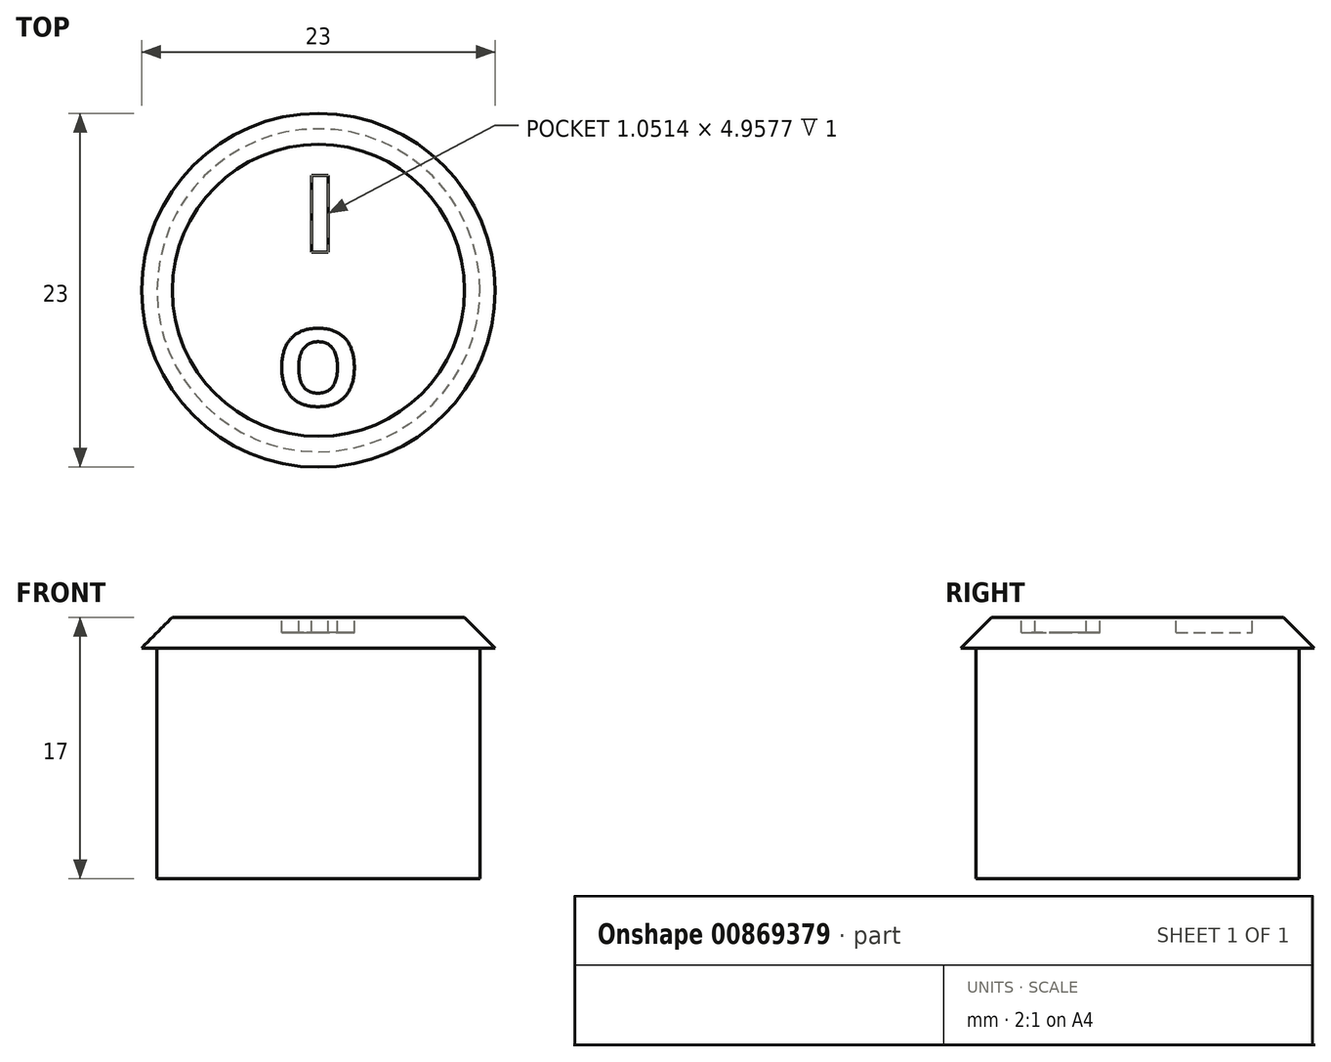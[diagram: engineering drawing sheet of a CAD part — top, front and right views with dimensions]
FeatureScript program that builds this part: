
annotation { "Feature Type Name" : "Feature", "Feature Type Description" : "" }
export const myFeature = defineFeature(function(context is Context, id is Id, definition is map)
    precondition{}
    {
        {
            var Q0;
            Q0=qCreatedBy(makeId("Front.planeOp"),FACE);
            var sketch = newSketch(context, id + "F0", { "sketchPlane" : qUnion([Q0])});
            skLineSegment(sketch, "E0", {"start": v(0, 17) * mm, "end": v(9.5, 17) * mm});
            skLineSegment(sketch, "E1", {"start": v(9.5, 17) * mm, "end": v(11.5, 15) * mm});
            skLineSegment(sketch, "E2", {"start": v(11.5, 15) * mm, "end": v(10.5, 15) * mm});
            skLineSegment(sketch, "E3", {"start": v(10.5, 15) * mm, "end": v(10.5, 0) * mm});
            skLineSegment(sketch, "E4", {"start": v(10.5, 0) * mm, "end": v(0, 0) * mm});
            skLineSegment(sketch, "E5", {"start": v(0, 0) * mm, "end": v(0, 17) * mm});
            skSolve(sketch);
        }
        {
            var Q0;
            Q0=makeQuery(id+"F0.imprint","IMPRINT",FACE,{"disambiguationData":[TD([[makeQuery(id+"F0.imprint","IMPRINT",EDGE,{"derivedFrom":sQuery(id+"F0.wireOp",EDGE,"E0")}),-1.0]])]});
            var Q1;
            Q1=sQuery(id+"F0.wireOp",EDGE,"E5");
            revolve(context, id + "F1", {"surfaceOperationType" : NewSurfaceOperationType.NEW, "entities" : qUnion([Q0]), "axis" : qUnion([Q1]), "revolveType" : RevolveType.FULL});
        }
        {
            var Q0;
            Q0=makeQuery(id+"F1.opRevolve","SWEPT_FACE",FACE,{"disambiguationData":[OSD([sQuery(id+"F0.wireOp",EDGE,"E0")])]});
            var sketch = newSketch(context, id + "F2", { "sketchPlane" : qUnion([Q0])});
            skText(sketch, "E6", { "text": "I", "fontName": "OpenSans-Bold.ttf"});
            skText(sketch, "E7", { "text": "O", "fontName": "OpenSans-Bold.ttf"});
            skLineSegment(sketch, "E8", {"start": v(-18.47, 0) * mm, "end": v(24.94, 0) * mm, "construction": true});
            skLineSegment(sketch, "E9", {"start": v(1.06, 2.5) * mm, "end": v(2.79, -2.5) * mm, "construction": true});
            skPoint(sketch, "E10", {"position": v(1.92, 0) * mm});
            const initialGuessF2  = {"E6": [-0.00106, 0.0025, 1, 0, 0.005], "E7": [-0.00279, -0.0075, 1, 0, 0.005]};
            skSetInitialGuess(sketch, initialGuessF2);
            skSolve(sketch);
        }
        {
            var Q0;
            Q0=makeQuery(id+"F2.imprint","IMPRINT",FACE,{"disambiguationData":[TD([[makeQuery(id+"F2.imprint","IMPRINT",EDGE,{"derivedFrom":sQuery(id+"F2.wireOp",EDGE,"E6.sketch_text.stroke-0")}),-1.0]])]});
            var Q1;
            Q1=makeQuery(id+"F2.imprint","IMPRINT",FACE,{"disambiguationData":[TD([[makeQuery(id+"F2.imprint","IMPRINT",EDGE,{"derivedFrom":sQuery(id+"F2.wireOp",EDGE,"E7.sketch_text.stroke-0")}),-1.0]])]});
            extrude(context, id + "F3", {"entities" : qUnion([Q0, Q1]), "operationType" : NewBodyOperationType.REMOVE, "oppositeDirection" : true, "depth" : 1 * mm, "offsetDistance" : 25 * mm});
        }
    });
